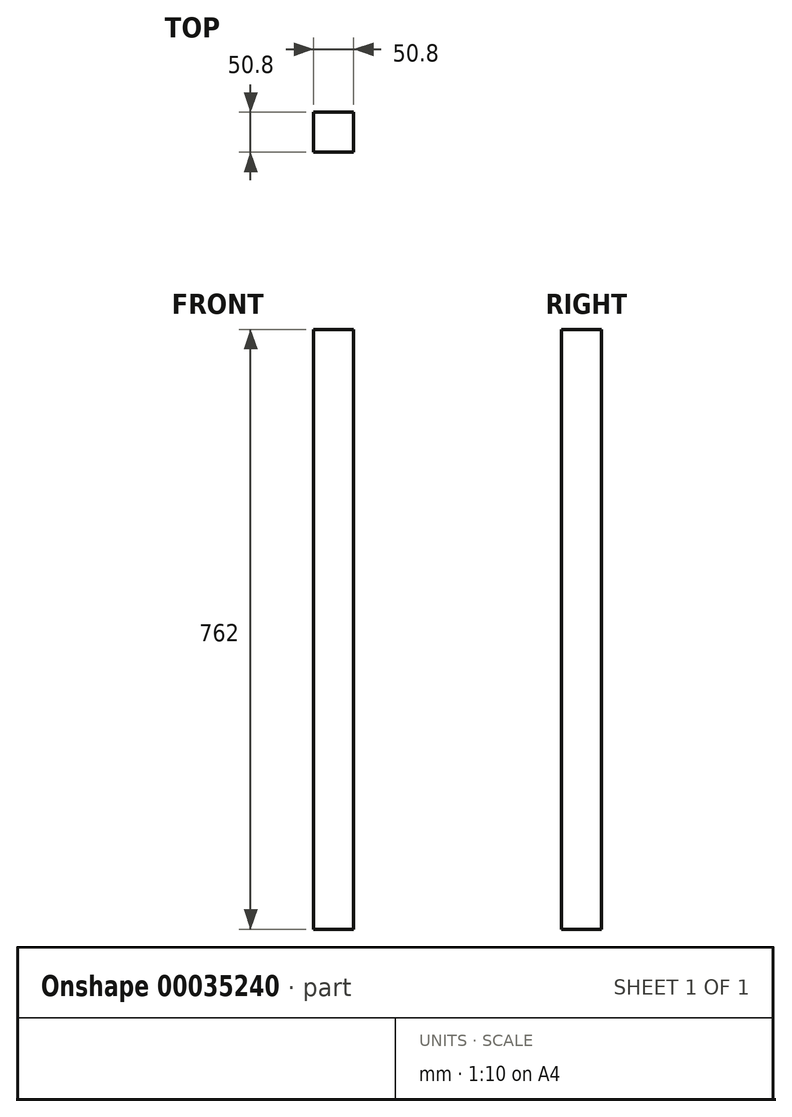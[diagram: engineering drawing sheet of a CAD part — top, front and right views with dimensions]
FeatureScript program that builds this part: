
annotation { "Feature Type Name" : "Feature", "Feature Type Description" : "" }
export const myFeature = defineFeature(function(context is Context, id is Id, definition is map)
    precondition{}
    {
        {
            var Q0;
            Q0=qCreatedBy(makeId("Top.planeOp"),FACE);
            var sketch = newSketch(context, id + "F0", { "sketchPlane" : qUnion([Q0])});
            skLineSegment(sketch, "E0.rect.bottom", {"start": v(25.4, -25.4) * mm, "end": v(-25.4, -25.4) * mm});
            skLineSegment(sketch, "E0.rect.top", {"start": v(25.4, 25.4) * mm, "end": v(-25.4, 25.4) * mm});
            skLineSegment(sketch, "E0.rect.left", {"start": v(25.4, -25.4) * mm, "end": v(25.4, 25.4) * mm});
            skLineSegment(sketch, "E0.rect.right", {"start": v(-25.4, -25.4) * mm, "end": v(-25.4, 25.4) * mm});
            skPoint(sketch, "E0.rect.middle", {"position": v(0, 0) * mm});
            skSolve(sketch);
        }
        {
            var Q0;
            Q0=makeQuery(id+"F0.imprint","IMPRINT",FACE,{"disambiguationData":[TD([[makeQuery(id+"F0.imprint","IMPRINT",EDGE,{"derivedFrom":sQuery(id+"F0.wireOp",EDGE,"E0.rect.bottom")}),-1.0]])]});
            extrude(context, id + "F1", {"entities" : qUnion([Q0]), "depth" : 762 * mm});
        }
    });
